# Revit family: ОВ_К_Р 1_Eng
name_source: partatom
category: Mechanical Equipment
units: mm (PartAtom-declared; Revit-internal decimal feet)

## family parameters
Always vertical = Yes
Classification = None
Cut with Voids When Loaded = No
Part Type = Normal
Room Calculation Point = No
Round Connector Dimension = Use Diameter
Shared = No
Work Plane-Based = No

## types (11) — shared parameters
00_20_Manufacturer = Vents
00_20_Name = Low pressure axial fans in the steel casing for wall mounting
Description = Low pressure axial fans in the steel casing for wall mounting
Frequency = 50 Hz
Load Classification = HVAC
Maintenance zone material = <By Category>
Manufacturer = Vents
Number of Fase = 1
URL = https://ventilation-system.com
Voltage = 230 V
d1 = 5 mm  [stored 0.0164042 ft]
l = 10 mm  [stored 0.0328084 ft]
t1 = 10 mm  [stored 0.0328084 ft]
zero-valued in all types: Default Elevation

## per-type parameters (varying)
- OV1 200: Amperage=0 A; Apparent Load=64 VA; B=312 mm; B1=260 mm; Casing Material=Metal, painted, matte black; D=208 mm; D1=198 mm; D11=193 mm; D111=186 mm; D1_1=63 mm  [stored 0.206693 ft]; D1_11=58 mm  [stored 0.190289 ft]; D2=183 mm; D22=178 mm; D222=213 mm; D2_2=48 mm  [stored 0.15748 ft]; D2_22=43 mm  [stored 0.141076 ft]; D3=168 mm; D33=163 mm; D3_3=33 mm  [stored 0.108268 ft]; D3_33=28 mm  [stored 0.0918635 ft]; D4=153 mm; D44=148 mm; D4_4=18 mm  [stored 0.0590551 ft]; D4_44=13 mm; D5=138 mm; D55=133 mm; D5_5=4 mm  [stored 0.0131234 ft]; D5_55=2 mm  [stored 0.00656168 ft]; D6=123 mm; D66=118 mm; D6_6=9 mm  [stored 0.0295276 ft]; D6_66=8 mm  [stored 0.0262467 ft]; D7=108 mm; D77=103 mm; D7_7=3 mm  [stored 0.00984252 ft]; D7_77=1 mm  [stored 0.00328084 ft]; D8=93 mm; D88=88 mm; D9=78 mm  [stored 0.255906 ft]; D99=73 mm  [stored 0.239501 ft]; Diameter=208 mm; Dy=203 mm; E2=119 mm; Grid OV1=Yes; Grid OV1 R=No; Grid OVК1=No; Height=312 mm; L=120 mm; Length=120 mm; Maximum Air Flow=405.0 m³/h; Partition=Yes; Power=43 W; Sound pressure level at 3 m distance=33 dBA; Weight=3.00 kg; Width=312 mm; d=7 mm  [stored 0.0229659 ft]; l1=104 mm; r=22 mm  [stored 0.0721785 ft]
- OV1 150: Amperage=0 A; Apparent Load=60 VA; B=250 mm; B1=210 mm; Casing Material=Metal, painted, matte black; D=162 mm; D1=152 mm; D11=147 mm; D111=186 mm; D1_1=17 mm; D1_11=12 mm  [stored 0.0393701 ft]; D2=137 mm; D22=132 mm; D222=167 mm; D2_2=2 mm  [stored 0.00656168 ft]; D2_22=3 mm  [stored 0.00984252 ft]; D3=122 mm; D33=117 mm; D3_3=6 mm  [stored 0.019685 ft]; D3_33=1 mm  [stored 0.00328084 ft]; D4=107 mm; D44=102 mm; D4_4=7 mm  [stored 0.0229659 ft]; D4_44=7 mm  [stored 0.0229659 ft]; D5=92 mm; D55=87 mm; D5_5=17 mm; D5_55=18 mm  [stored 0.0590551 ft]; D6=77 mm  [stored 0.252625 ft]; D66=72 mm  [stored 0.23622 ft]; D6_6=27 mm  [stored 0.0885827 ft]; D6_66=28 mm  [stored 0.0918635 ft]; D7=62 mm  [stored 0.203412 ft]; D77=57 mm  [stored 0.187008 ft]; D7_7=47 mm  [stored 0.154199 ft]; D7_77=48 mm  [stored 0.15748 ft]; D8=47 mm  [stored 0.154199 ft]; D88=42 mm  [stored 0.137795 ft]; D9=32 mm  [stored 0.104987 ft]; D99=27 mm  [stored 0.0885827 ft]; Diameter=162 mm; Dy=157 mm; E2=96 mm; Grid OV1=Yes; Grid OV1 R=No; Grid OVК1=No; Height=250 mm; L=120 mm; Length=120 mm; Maximum Air Flow=200.0 m³/h; Partition=Yes; Power=36 W; Sound pressure level at 3 m distance=33 dBA; Weight=2.50 kg; Width=250 mm; d=7 mm  [stored 0.0229659 ft]; l1=81 mm  [stored 0.265748 ft]; r=18 mm  [stored 0.0590551 ft]
- OV1 250: Amperage=0 A; Apparent Load=110 VA; B=370 mm; B1=320 mm; Casing Material=Metal, painted, matte black; D=262 mm; D1=252 mm; D11=247 mm; D111=186 mm; D1_1=117 mm; D1_11=112 mm; D2=237 mm; D22=232 mm; D222=267 mm; D2_2=102 mm; D2_22=97 mm; D3=222 mm; D33=217 mm; D3_3=87 mm; D3_33=82 mm  [stored 0.269029 ft]; D4=207 mm; D44=202 mm; D4_4=72 mm  [stored 0.23622 ft]; D4_44=67 mm; D5=192 mm; D55=187 mm; D5_5=57 mm  [stored 0.187008 ft]; D5_55=52 mm; D6=177 mm; D66=172 mm; D6_6=42 mm  [stored 0.137795 ft]; D6_66=37 mm  [stored 0.121391 ft]; D7=162 mm; D77=157 mm; D7_7=27 mm  [stored 0.0885827 ft]; D7_77=22 mm  [stored 0.0721785 ft]; D8=147 mm; D88=142 mm; D9=132 mm; D99=127 mm; Diameter=262 mm; Dy=257 mm; E2=146 mm; Grid OV1=Yes; Grid OV1 R=No; Grid OVК1=No; Height=370 mm; L=140 mm; Length=140 mm; Maximum Air Flow=1070.0 m³/h; Partition=Yes; Power=68 W; Sound pressure level at 3 m distance=37 dBA; Weight=3.50 kg; Width=370 mm; d=7 mm  [stored 0.0229659 ft]; l1=131 mm; r=26 mm
- OV1 315: Amperage=1 A; Apparent Load=173 VA; B=430 mm; B1=380 mm; Casing Material=Metal, painted, matte black; D=312 mm; D1=302 mm; D11=297 mm; D111=186 mm; D1_1=167 mm; D1_11=162 mm; D2=287 mm; D22=282 mm; D222=317 mm; D2_2=152 mm; D2_22=147 mm; D3=272 mm; D33=267 mm; D3_3=137 mm; D3_33=132 mm; D4=257 mm; D44=252 mm; D4_4=122 mm; D4_44=117 mm; D5=242 mm; D55=237 mm; D5_5=107 mm; D5_55=102 mm; D6=227 mm; D66=222 mm; D6_6=92 mm; D6_66=87 mm; D7=212 mm; D77=207 mm; D7_7=77 mm  [stored 0.252625 ft]; D7_77=72 mm  [stored 0.23622 ft]; D8=197 mm; D88=192 mm; D9=182 mm; D99=177 mm; Diameter=312 mm; Dy=307 mm; E2=171 mm; Grid OV1=Yes; Grid OV1 R=No; Grid OVК1=No; Height=430 mm; L=170 mm; Length=170 mm; Maximum Air Flow=1700.0 m³/h; Partition=Yes; Power=110 W; Sound pressure level at 3 m distance=42 dBA; Weight=6.10 kg; Width=430 mm; d=9 mm  [stored 0.0295276 ft]; l1=156 mm; r=30 mm  [stored 0.0984252 ft]
- OVK1 150: Amperage=0 A; Apparent Load=60 VA; B=250 mm; B1=210 mm; Casing Material=Metal, painted, matte black; D=162 mm; D1=152 mm; D11=147 mm; D111=190 mm; D1_1=17 mm; D1_11=12 mm  [stored 0.0393701 ft]; D2=137 mm; D22=132 mm; D222=220 mm; D2_2=2 mm  [stored 0.00656168 ft]; D2_22=3 mm  [stored 0.00984252 ft]; D3=122 mm; D33=117 mm; D3_3=6 mm  [stored 0.019685 ft]; D3_33=1 mm  [stored 0.00328084 ft]; D4=107 mm; D44=102 mm; D4_4=7 mm  [stored 0.0229659 ft]; D4_44=7 mm  [stored 0.0229659 ft]; D5=92 mm; D55=87 mm; D5_5=17 mm; D5_55=18 mm  [stored 0.0590551 ft]; D6=77 mm  [stored 0.252625 ft]; D66=72 mm  [stored 0.23622 ft]; D6_6=27 mm  [stored 0.0885827 ft]; D6_66=28 mm  [stored 0.0918635 ft]; D7=62 mm  [stored 0.203412 ft]; D77=57 mm  [stored 0.187008 ft]; D7_7=47 mm  [stored 0.154199 ft]; D7_77=48 mm  [stored 0.15748 ft]; D8=47 mm  [stored 0.154199 ft]; D88=42 mm  [stored 0.137795 ft]; D9=32 mm  [stored 0.104987 ft]; D99=27 mm  [stored 0.0885827 ft]; Diameter=220 mm; Dy=157 mm; E2=96 mm; Grid OV1=No; Grid OV1 R=No; Grid OVК1=Yes; Height=220 mm; L=120 mm; Length=120 mm; Maximum Air Flow=200.0 m³/h; Partition=Yes; Power=36 W; Sound pressure level at 3 m distance=33 dBA; Weight=2.50 kg; Width=220 mm; d=7 mm  [stored 0.0229659 ft]; l1=81 mm  [stored 0.265748 ft]; r=18 mm  [stored 0.0590551 ft]
- OVK1 200: Amperage=0 A; Apparent Load=64 VA; B=312 mm; B1=260 mm; Casing Material=Metal, painted, matte black; D=208 mm; D1=198 mm; D11=193 mm; D111=270 mm; D1_1=63 mm  [stored 0.206693 ft]; D1_11=58 mm  [stored 0.190289 ft]; D2=183 mm; D22=178 mm; D222=300 mm; D2_2=48 mm  [stored 0.15748 ft]; D2_22=43 mm  [stored 0.141076 ft]; D3=168 mm; D33=163 mm; D3_3=33 mm  [stored 0.108268 ft]; D3_33=28 mm  [stored 0.0918635 ft]; D4=153 mm; D44=148 mm; D4_4=18 mm  [stored 0.0590551 ft]; D4_44=13 mm; D5=138 mm; D55=133 mm; D5_5=4 mm  [stored 0.0131234 ft]; D5_55=2 mm  [stored 0.00656168 ft]; D6=123 mm; D66=118 mm; D6_6=9 mm  [stored 0.0295276 ft]; D6_66=8 mm  [stored 0.0262467 ft]; D7=108 mm; D77=103 mm; D7_7=3 mm  [stored 0.00984252 ft]; D7_77=1 mm  [stored 0.00328084 ft]; D8=93 mm; D88=88 mm; D9=78 mm  [stored 0.255906 ft]; D99=73 mm  [stored 0.239501 ft]; Diameter=300 mm; Dy=203 mm; E2=119 mm; Grid OV1=No; Grid OV1 R=No; Grid OVК1=Yes; Height=300 mm; L=120 mm; Length=120 mm; Maximum Air Flow=405.0 m³/h; Partition=Yes; Power=43 W; Sound pressure level at 3 m distance=33 dBA; Weight=2.50 kg; Width=300 mm; d=7 mm  [stored 0.0229659 ft]; l1=104 mm; r=22 mm  [stored 0.0721785 ft]
- OVK1 250: Amperage=0 A; Apparent Load=110 VA; B=370 mm; B1=320 mm; Casing Material=Metal, painted, matte black; D=262 mm; D1=252 mm; D11=247 mm; D111=330 mm; D1_1=117 mm; D1_11=112 mm; D2=237 mm; D22=232 mm; D222=360 mm; D2_2=102 mm; D2_22=97 mm; D3=222 mm; D33=217 mm; D3_3=87 mm; D3_33=82 mm  [stored 0.269029 ft]; D4=207 mm; D44=202 mm; D4_4=72 mm  [stored 0.23622 ft]; D4_44=67 mm; D5=192 mm; D55=187 mm; D5_5=57 mm  [stored 0.187008 ft]; D5_55=52 mm; D6=177 mm; D66=172 mm; D6_6=42 mm  [stored 0.137795 ft]; D6_66=37 mm  [stored 0.121391 ft]; D7=162 mm; D77=157 mm; D7_7=27 mm  [stored 0.0885827 ft]; D7_77=22 mm  [stored 0.0721785 ft]; D8=147 mm; D88=142 mm; D9=132 mm; D99=127 mm; Diameter=360 mm; Dy=257 mm; E2=146 mm; Grid OV1=No; Grid OV1 R=No; Grid OVК1=Yes; Height=360 mm; L=140 mm; Length=140 mm; Maximum Air Flow=1070.0 m³/h; Partition=Yes; Power=68 W; Sound pressure level at 3 m distance=37 dBA; Weight=3.00 kg; Width=360 mm; d=7 mm  [stored 0.0229659 ft]; l1=131 mm; r=26 mm
- OVK1 315: Amperage=1 A; Apparent Load=173 VA; B=430 mm; B1=380 mm; Casing Material=Metal, painted, matte black; D=312 mm; D1=302 mm; D11=297 mm; D111=390 mm; D1_1=167 mm; D1_11=162 mm; D2=287 mm; D22=282 mm; D222=420 mm; D2_2=152 mm; D2_22=147 mm; D3=272 mm; D33=267 mm; D3_3=137 mm; D3_33=132 mm; D4=257 mm; D44=252 mm; D4_4=122 mm; D4_44=117 mm; D5=242 mm; D55=237 mm; D5_5=107 mm; D5_55=102 mm; D6=227 mm; D66=222 mm; D6_6=92 mm; D6_66=87 mm; D7=212 mm; D77=207 mm; D7_7=77 mm  [stored 0.252625 ft]; D7_77=72 mm  [stored 0.23622 ft]; D8=197 mm; D88=192 mm; D9=182 mm; D99=177 mm; Diameter=420 mm; Dy=307 mm; E2=171 mm; Grid OV1=No; Grid OV1 R=No; Grid OVК1=Yes; Height=420 mm; L=170 mm; Length=170 mm; Maximum Air Flow=1700.0 m³/h; Partition=Yes; Power=110 W; Sound pressure level at 3 m distance=42 dBA; Weight=5.10 kg; Width=420 mm; d=9 mm  [stored 0.0295276 ft]; l1=156 mm; r=30 mm  [stored 0.0984252 ft]
- OV1 150 R: Amperage=0 A; Apparent Load=60 VA; B=325 mm; B1=210 mm; Casing Material=Plastic, opaque, white; D=162 mm; D1=152 mm; D11=147 mm; D111=190 mm; D1_1=17 mm; D1_11=12 mm  [stored 0.0393701 ft]; D2=137 mm; D22=132 mm; D222=220 mm; D2_2=2 mm  [stored 0.00656168 ft]; D2_22=3 mm  [stored 0.00984252 ft]; D3=122 mm; D33=117 mm; D3_3=6 mm  [stored 0.019685 ft]; D3_33=1 mm  [stored 0.00328084 ft]; D4=107 mm; D44=102 mm; D4_4=7 mm  [stored 0.0229659 ft]; D4_44=7 mm  [stored 0.0229659 ft]; D5=92 mm; D55=87 mm; D5_5=17 mm; D5_55=18 mm  [stored 0.0590551 ft]; D6=77 mm  [stored 0.252625 ft]; D66=72 mm  [stored 0.23622 ft]; D6_6=27 mm  [stored 0.0885827 ft]; D6_66=28 mm  [stored 0.0918635 ft]; D7=62 mm  [stored 0.203412 ft]; D77=57 mm  [stored 0.187008 ft]; D7_7=47 mm  [stored 0.154199 ft]; D7_77=48 mm  [stored 0.15748 ft]; D8=47 mm  [stored 0.154199 ft]; D88=42 mm  [stored 0.137795 ft]; D9=32 mm  [stored 0.104987 ft]; D99=27 mm  [stored 0.0885827 ft]; Diameter=162 mm; Dy=157 mm; E2=96 mm; Grid OV1=No; Grid OV1 R=Yes; Grid OVК1=No; Height=325 mm; L=127 mm; Length=127 mm; Maximum Air Flow=200.0 m³/h; Partition=No; Power=36 W; Sound pressure level at 3 m distance=33 dBA; Weight=2.50 kg; Width=325 mm; d=7 mm  [stored 0.0229659 ft]; l1=81 mm  [stored 0.265748 ft]; r=23 mm  [stored 0.0754593 ft]
- OV1 200 R: Amperage=0 A; Apparent Load=64 VA; B=325 mm; B1=210 mm; Casing Material=Plastic, opaque, white; D=208 mm; D1=198 mm; D11=193 mm; D111=190 mm; D1_1=63 mm  [stored 0.206693 ft]; D1_11=58 mm  [stored 0.190289 ft]; D2=183 mm; D22=178 mm; D222=220 mm; D2_2=48 mm  [stored 0.15748 ft]; D2_22=43 mm  [stored 0.141076 ft]; D3=168 mm; D33=163 mm; D3_3=33 mm  [stored 0.108268 ft]; D3_33=28 mm  [stored 0.0918635 ft]; D4=153 mm; D44=148 mm; D4_4=18 mm  [stored 0.0590551 ft]; D4_44=13 mm; D5=138 mm; D55=133 mm; D5_5=4 mm  [stored 0.0131234 ft]; D5_55=2 mm  [stored 0.00656168 ft]; D6=123 mm; D66=118 mm; D6_6=9 mm  [stored 0.0295276 ft]; D6_66=8 mm  [stored 0.0262467 ft]; D7=108 mm; D77=103 mm; D7_7=3 mm  [stored 0.00984252 ft]; D7_77=1 mm  [stored 0.00328084 ft]; D8=93 mm; D88=88 mm; D9=78 mm  [stored 0.255906 ft]; D99=73 mm  [stored 0.239501 ft]; Diameter=208 mm; Dy=203 mm; E2=119 mm; Grid OV1=No; Grid OV1 R=Yes; Grid OVК1=No; Height=325 mm; L=127 mm; Length=127 mm; Maximum Air Flow=405.0 m³/h; Partition=No; Power=43 W; Sound pressure level at 3 m distance=32 dBA; Weight=3.00 kg; Width=325 mm; d=7 mm  [stored 0.0229659 ft]; l1=104 mm; r=23 mm  [stored 0.0754593 ft]
- OV1 250 R: Amperage=0 A; Apparent Load=110 VA; B=325 mm; B1=320 mm; Casing Material=Plastic, opaque, white; D=262 mm; D1=252 mm; D11=247 mm; D111=186 mm; D1_1=117 mm; D1_11=112 mm; D2=237 mm; D22=232 mm; D222=267 mm; D2_2=102 mm; D2_22=97 mm; D3=222 mm; D33=217 mm; D3_3=87 mm; D3_33=82 mm  [stored 0.269029 ft]; D4=207 mm; D44=202 mm; D4_4=72 mm  [stored 0.23622 ft]; D4_44=67 mm; D5=192 mm; D55=187 mm; D5_5=57 mm  [stored 0.187008 ft]; D5_55=52 mm; D6=177 mm; D66=172 mm; D6_6=42 mm  [stored 0.137795 ft]; D6_66=37 mm  [stored 0.121391 ft]; D7=162 mm; D77=157 mm; D7_7=27 mm  [stored 0.0885827 ft]; D7_77=22 mm  [stored 0.0721785 ft]; D8=147 mm; D88=142 mm; D9=132 mm; D99=127 mm; Diameter=262 mm; Dy=257 mm; E2=146 mm; Grid OV1=No; Grid OV1 R=Yes; Grid OVК1=No; Height=325 mm; L=152 mm; Length=152 mm; Maximum Air Flow=1070.0 m³/h; Partition=No; Power=68 W; Sound pressure level at 3 m distance=37 dBA; Weight=3.50 kg; Width=325 mm; d=7 mm  [stored 0.0229659 ft]; l1=131 mm; r=23 mm  [stored 0.0754593 ft]

note: column(s) folded — value = type name in every type: 00_20_Type

note: [stored X ft] marks values corroborated as IEEE doubles in the binary element streams (Revit-internal decimal feet)
